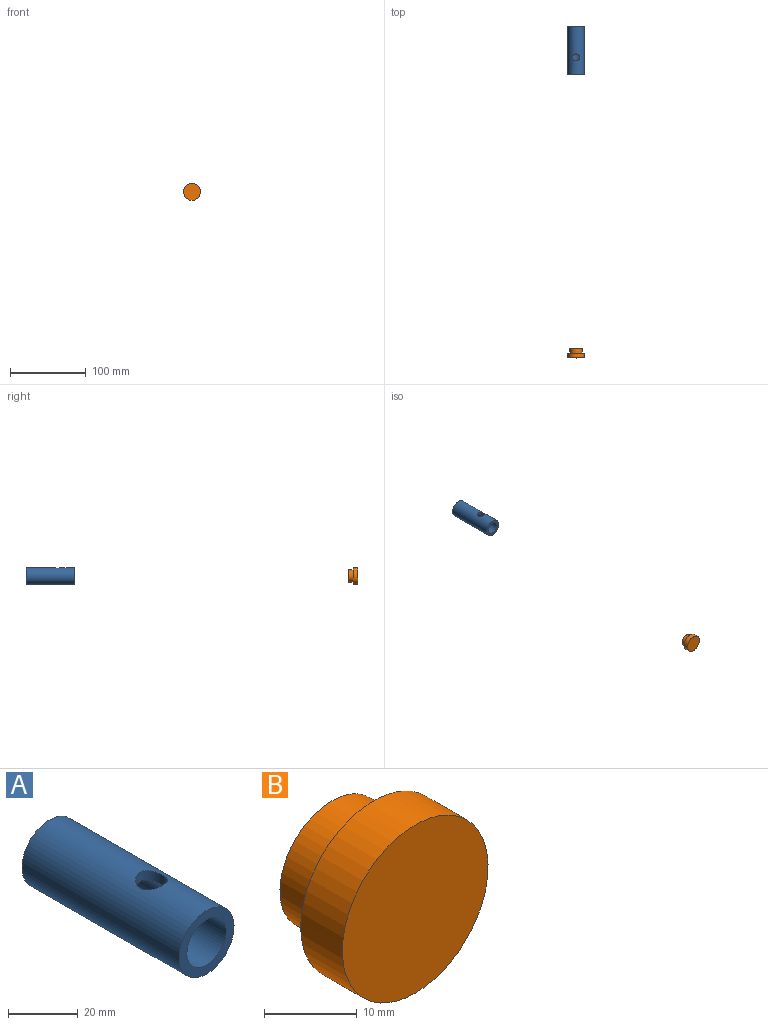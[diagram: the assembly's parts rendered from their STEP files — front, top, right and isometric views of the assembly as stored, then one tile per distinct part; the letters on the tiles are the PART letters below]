
ASSEMBLY  parts=2 mates=1
PART A: 5 faces, bbox 22.2x63.5x22.2 mm
  f0: cylinder r=7.94mm len=63.5mm, axis (0,1,0), area 3098.5mm2, adj f2,f3,f4
  f1: cylinder r=11.11mm len=63.5mm, axis (0,1,0), area 4366.9mm2, adj f2,f3,f4
  f2: plane 22.23x22.23mm, normal (0,1,0), area 190mm2, adj f0,f1
  f3: cylinder r=4.56mm len=9.13mm, axis (0,0,1), area 97.3mm2, adj f0,f1
  f4: plane 22.23x22.23mm, normal (0,-1,0), area 190mm2, adj f0,f1
PART B: 5 faces, bbox 22.2x12.7x22.2 mm
  f0: cylinder r=7.94mm len=15.88mm, axis (0,1,0), area 316.7mm2, adj f1,f4
  f1: plane 15.88x15.88mm, normal (0,1,0), area 197.9mm2, adj f0
  f2: cylinder r=11.11mm len=22.23mm, axis (0,1,0), area 443.4mm2, adj f3,f4
  f3: plane 22.23x22.23mm, normal (0,-1,0), area 387.9mm2, adj f2
  f4: plane 22.23x22.23mm, normal (0,1,0), area 190mm2, adj f0,f2
PLACE A t=(-14.72,-6.54,-3.04)mm
PLACE B t=(-14.72,-430.66,-3.04)mm
MATE slider B.f0 <-> A.f0  axis (0,1,0) through (-14.72,-430.66,-3.04)mm
